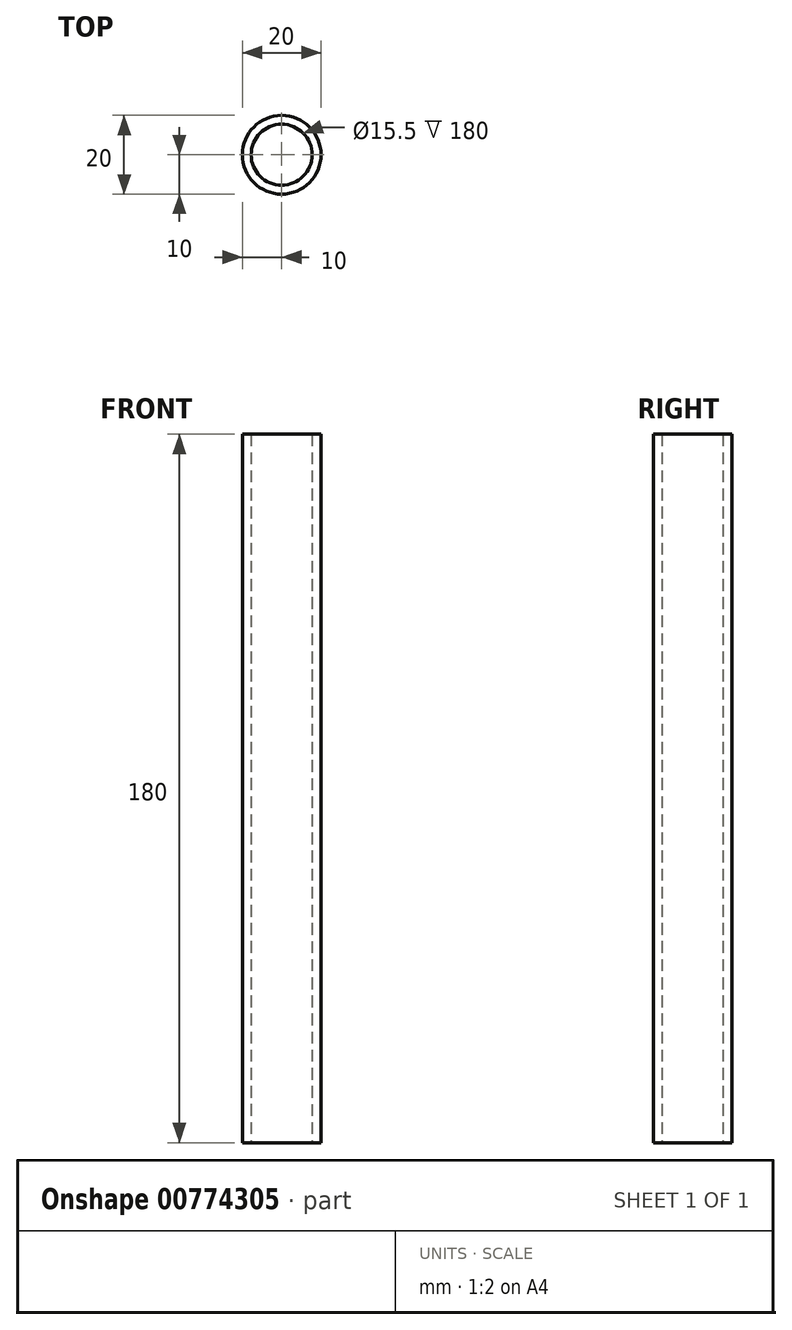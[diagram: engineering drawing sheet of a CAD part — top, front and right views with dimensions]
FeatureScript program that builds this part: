
annotation { "Feature Type Name" : "Feature", "Feature Type Description" : "" }
export const myFeature = defineFeature(function(context is Context, id is Id, definition is map)
    precondition{}
    {
        {
            var Q0;
            Q0=qCreatedBy(makeId("Top.planeOp"),FACE);
            var sketch = newSketch(context, id + "F0", { "sketchPlane" : qUnion([Q0])});
            skCircle(sketch, "E0", {"center": v(0, 0) * mm, "radius": 7.75 * mm});
            skCircle(sketch, "E1", {"center": v(0, 0) * mm, "radius": 10 * mm});
            skSolve(sketch);
        }
        {
            var Q0;
            Q0 = qSketchRegion(id + "F0", true);
            extrude(context, id + "F1", {"entities" : qUnion([Q0]), "depth" : 180 * mm, "offsetDistance" : 25 * mm});
        }
    });
